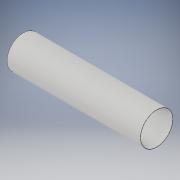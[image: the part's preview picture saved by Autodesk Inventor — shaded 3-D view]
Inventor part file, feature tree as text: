
AUTODESK INVENTOR PART (.ipt)
format: ipt  version: 2019 (Build 230136000, 136)  size: 98,304 bytes
history: native  units: in
note: dims shown in document units (in); Inventor stores cm internally (conversion verified against a paired STEP export)
features: extrude x2, sketch x2
ambient origin geometry x8: Origin, YZ Plane, XZ Plane, XY Plane, X Axis, Y Axis, Z Axis, Center Point
bodies: Solid1 (feature_tree)
feature tree (4):
  extrude  "Extrusion1"  Depth=6.9291in TaperAngle=0.0deg
  extrude  "Extrusion2"  [1 undecoded]
  sketch  "Sketch1"  dims[d0=1.6929in d1=6.9291in d2=0.0in]
  sketch  "Sketch2"  dims[d4=6.9291in d5=0.0in]
note: 1 required parameter value undecoded (feature->parameter linkage not recoverable at this tier; creation-order binding heuristic only, values carry confidence <= 0.55)
